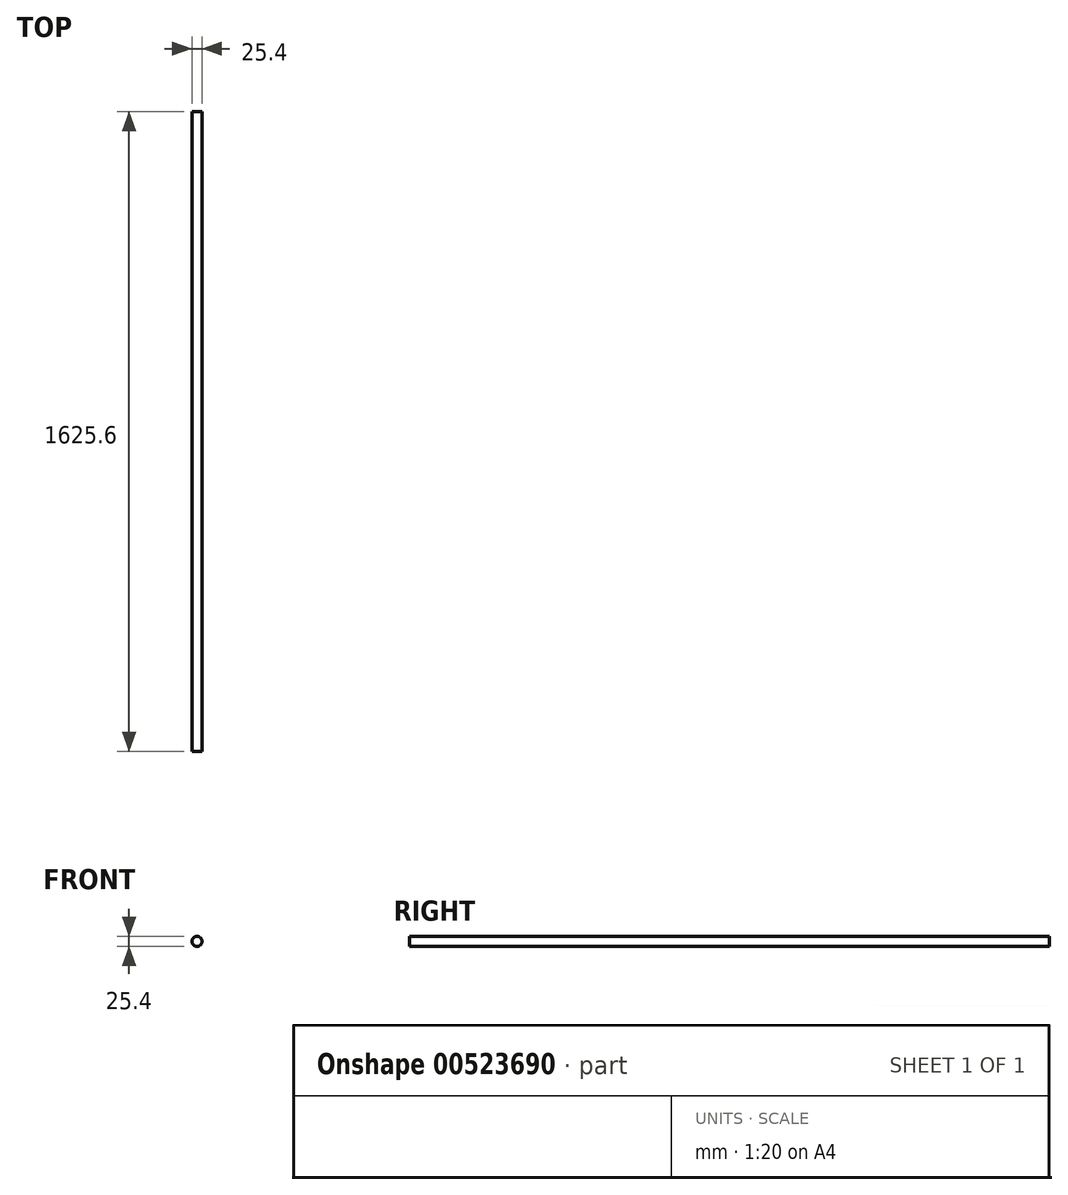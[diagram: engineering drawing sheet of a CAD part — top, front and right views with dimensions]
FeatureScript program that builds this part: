
annotation { "Feature Type Name" : "Feature", "Feature Type Description" : "" }
export const myFeature = defineFeature(function(context is Context, id is Id, definition is map)
    precondition{}
    {
        {
            var Q0;
            Q0=qCreatedBy(makeId("Front.planeOp"),FACE);
            var sketch = newSketch(context, id + "F0", { "sketchPlane" : qUnion([Q0])});
            skCircle(sketch, "E0", {"center": v(0, 0) * mm, "radius": 12.7 * mm});
            skSolve(sketch);
        }
        {
            var Q0;
            Q0 = qSketchRegion(id + "F0", true);
            extrude(context, id + "F1", {"entities" : qUnion([Q0]), "depth" : 1625.6 * mm, "offsetDistance" : 25.4 * mm});
        }
    });
